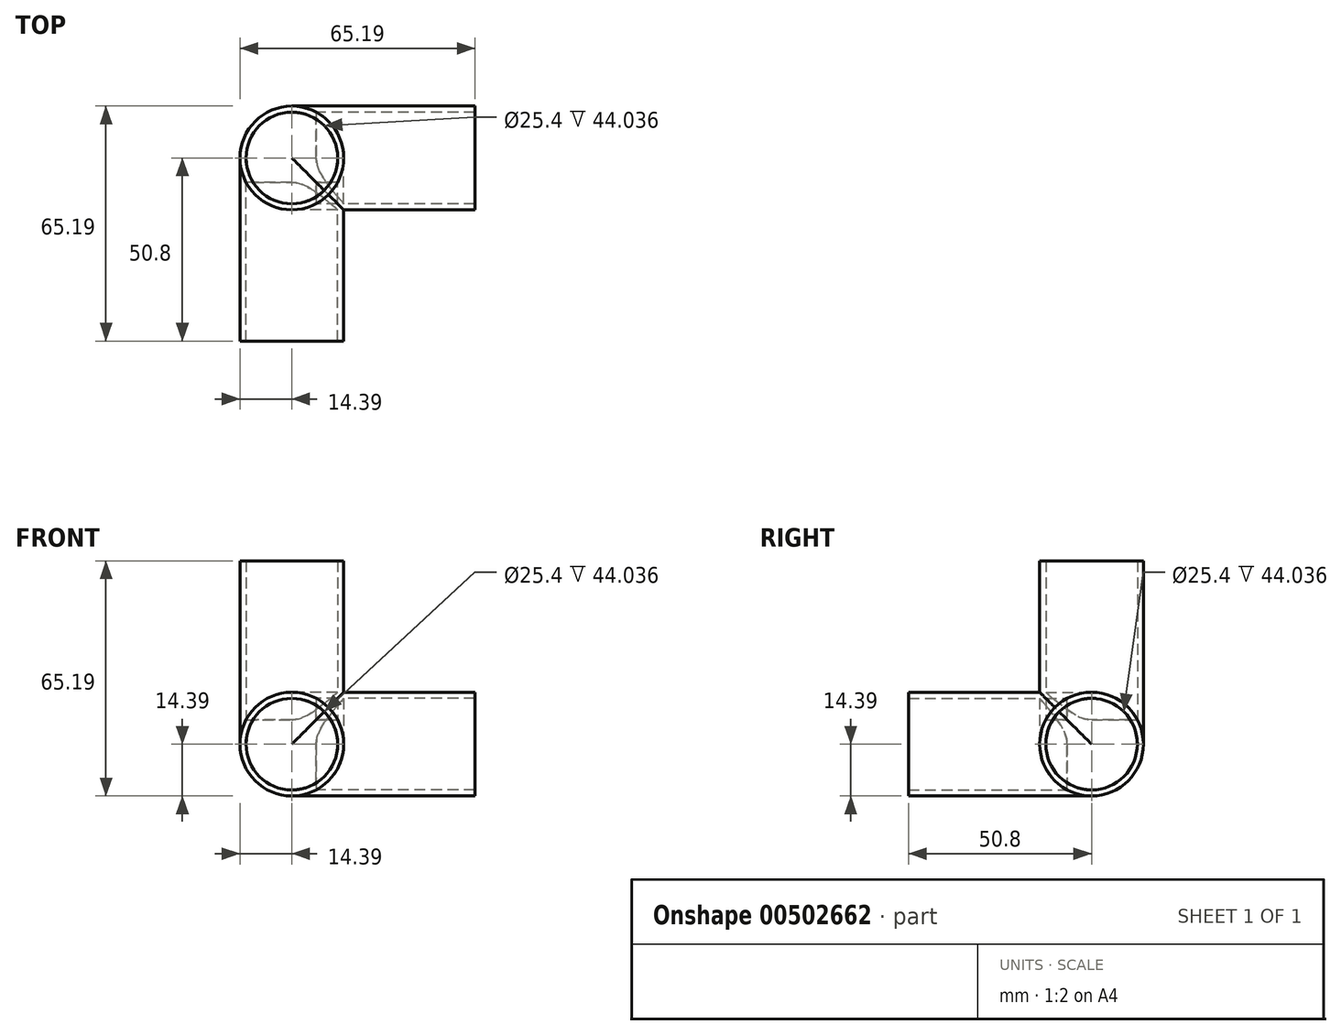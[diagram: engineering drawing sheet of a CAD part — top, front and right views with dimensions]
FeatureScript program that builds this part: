
annotation { "Feature Type Name" : "Feature", "Feature Type Description" : "" }
export const myFeature = defineFeature(function(context is Context, id is Id, definition is map)
    precondition{}
    {
        {
            var Q0;
            Q0=qCreatedBy(makeId("Front.planeOp"),FACE);
            var sketch = newSketch(context, id + "F0", { "sketchPlane" : qUnion([Q0])});
            skCircle(sketch, "E0", {"center": v(0, 0) * mm, "radius": 14.39 * mm});
            skCircle(sketch, "E1", {"center": v(0, 0) * mm, "radius": 12.7 * mm});
            skSolve(sketch);
        }
        {
            var Q0;
            Q0=qSketchRegion(id+"F0",true);
            extrude(context, id + "F1", {"entities" : qUnion([Q0]), "depth" : 50.8 * mm});
        }
        {
            var Q0;
            Q0=qCreatedBy(makeId("Right.planeOp"),FACE);
            var sketch = newSketch(context, id + "F2", { "sketchPlane" : qUnion([Q0])});
            skCircle(sketch, "E2", {"center": v(0, 0) * mm, "radius": 14.39 * mm});
            skCircle(sketch, "E3", {"center": v(0, 0) * mm, "radius": 12.7 * mm});
            skSolve(sketch);
        }
        {
            var Q0;
            Q0=qSketchRegion(id+"F2",true);
            extrude(context, id + "F3", {"entities" : qUnion([Q0]), "operationType" : NewBodyOperationType.ADD, "depth" : 50.8 * mm});
        }
        {
            var Q0;
            Q0=qCreatedBy(makeId("Top.planeOp"),FACE);
            var sketch = newSketch(context, id + "F4", { "sketchPlane" : qUnion([Q0])});
            skCircle(sketch, "E4", {"center": v(0, 0) * mm, "radius": 14.39 * mm});
            skCircle(sketch, "E5", {"center": v(0, 0) * mm, "radius": 12.7 * mm});
            skSolve(sketch);
        }
        {
            var Q0;
            Q0=qSketchRegion(id+"F4",true);
            extrude(context, id + "F5", {"entities" : qUnion([Q0]), "operationType" : NewBodyOperationType.ADD, "depth" : 50.8 * mm});
        }
        {
            var Q0;
            Q0=qCreatedBy(makeId("Front.planeOp"),FACE);
            var sketch = newSketch(context, id + "F6", { "sketchPlane" : qUnion([Q0])});
            skLineSegment(sketch, "E6", {"start": v(-14.39, 0) * mm, "end": v(14.39, 0) * mm});
            skArc(sketch, "E7", {"start": v(14.39, 0) * mm, "mid": v(0, 14.39) * mm, "end": v(-14.39, 0) * mm});
            skSolve(sketch);
        }
        {
            var Q0;
            Q0=makeQuery(id+"F6.imprint","IMPRINT",FACE,{"disambiguationData":[TD([[makeQuery(id+"F6.imprint","IMPRINT",EDGE,{"derivedFrom":sQuery(id+"F6.wireOp",EDGE,"E6")}),1.0]])]});
            var Q1;
            Q1=sQuery(id+"F6.wireOp",EDGE,"E6");
            revolve(context, id + "F7", {"operationType" : NewBodyOperationType.ADD, "entities" : qUnion([Q0]), "axis" : qUnion([Q1]), "revolveType" : RevolveType.FULL});
        }
    });
